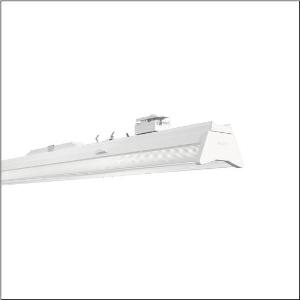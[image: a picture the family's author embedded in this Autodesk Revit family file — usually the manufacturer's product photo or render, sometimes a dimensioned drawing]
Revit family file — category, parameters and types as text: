
# Revit family: licross_r__21_performance_mo_52tm167n46xg_7cd2
name_source: partatom
category: Lighting Fixtures
units: mm (PartAtom-declared; Revit-internal decimal feet)

## family parameters
Cut with Voids When Loaded = No
Host = Face
Light Source = No
Part Type = Normal
Room Calculation Point = No
Round Connector Dimension = Use Diameter
Shared = No

## types (1)
- Licross® 21 Performance MO (1 x LED, 6000 lm, 32.4 W, 4000K)
    Apparent Load = 32 VA
    CIE Flux Codes = 66 88 96 79 100
    Color Rendering = 80
    Color Temperature = 4000K
    Default Elevation = 1800 mm
    Description = Licross® 21 Performance MO, luminaire insert, of sheet steel, galvanised, coil coated, white, length: 1.500mm, width: 120mm, height: 123mm, LED rated luminous flux: 6.000lm, light colour: 840, control gear: ON/OFF, with plug, 3-pole, with phase selection, mains connection: 220..240V, AC, 50/60Hz, rated input power: 32W, halogen-free wiring, primary light control with lens, of plastic, primary optical cover: cover, of PMMA, light emission: direct/indirect distribution, primary light characteristic: symmetric, protection rating (complete): IP40, insulation class (complete): insulation class I (protective earthing), certification: CE, ENEC, UKCA, protection symbol: D if used in an environment without relevant dust loads with corresponding accessories, impact resistance: IK06, permissible ambient temperature for indoor applications: -35..+50°C, corresponds to IFS (International Featured Standards) requirements for safety and quality in the food industry, reducing of maximum allowable ambient temperature of 5°C with ceiling mounting, LABS conformity tested according to VDMA 24364:2018-05, packaging unit: 1 piece
    Height = 114 mm
    Lamp = 1 x LED
    Lamp Light Flux = 6000 lm
    Lamp Power = 32.4 W
    Lamp count = 1
    Length = 1500 mm
    Luminous efficacy = 185 lm/W
    Manufacturer = Siteco
    ModVariant = No
    Model = 52TM167N46XG
    Mounting Place = Ceiling
    Mounting Type = Pendant
    Number of Poles = 1
    OnlyDefault = Yes
    Power Factor = 1
    Product Name = Licross® 21 Performance MO
    Product group = luminaire insert
    ProductGroupID = 901
    Protection Class = Protection class I
    Protection Degree = IP 40
    RLX_Detail_Level = 1
    RLX_Emergency_Light_Flux = 0 lm
    RLX_Emergency_Type = 0
    RLX_Emergency_Type_DB = No
    RlxData = <blob elided: 30405 chars, md5=fb64c365>
    Socket = socket
    Standby Power = 0 W
    System Light Flux = 6000 lm
    System Power = 32 W
    Type Comments = Product without accessories
    Type Image = l_1256138.jpg
    URL = http://relux.com
    VarID = ---
    Voltage = 0 V
    Weight = 0.00 kg
    Width = 120 mm

## geometry (parser evidence)
native form markers: Blend x4, Sweep x14
no freeform markers — native parametric forms only
